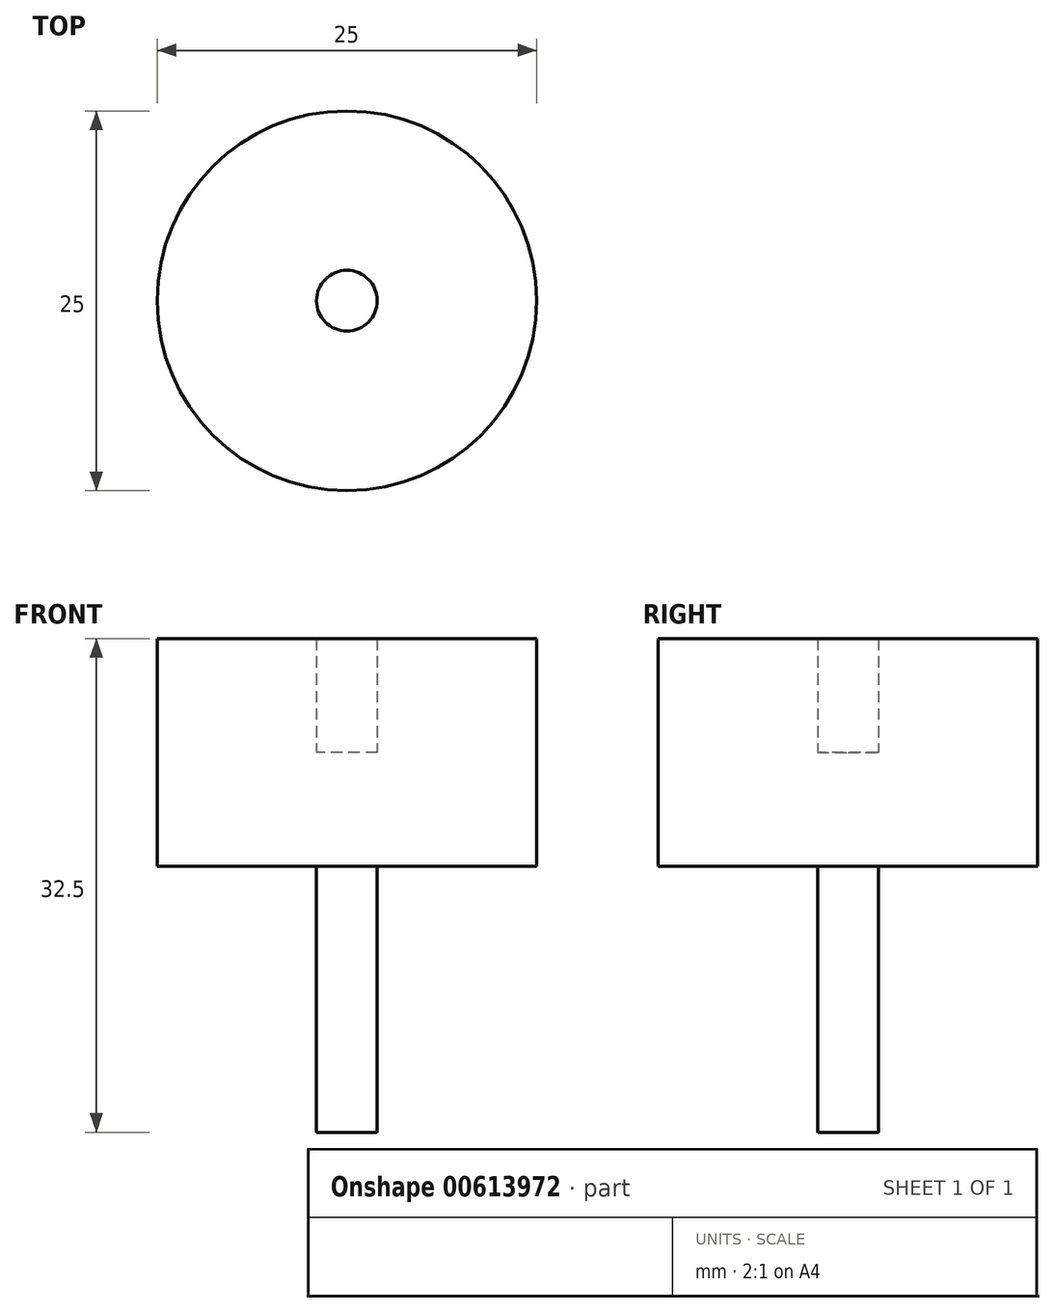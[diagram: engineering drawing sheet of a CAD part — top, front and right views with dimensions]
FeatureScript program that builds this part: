
annotation { "Feature Type Name" : "Feature", "Feature Type Description" : "" }
export const myFeature = defineFeature(function(context is Context, id is Id, definition is map)
    precondition{}
    {
        {
            var Q0;
            Q0=qCreatedBy(makeId("Top.planeOp"),FACE);
            var sketch = newSketch(context, id + "F0", { "sketchPlane" : qUnion([Q0])});
            skCircle(sketch, "E0", {"center": v(0, 0) * mm, "radius": 2 * mm});
            skSolve(sketch);
        }
        {
            var Q0;
            Q0 = qSketchRegion(id + "F0", true);
            extrude(context, id + "F1", {"entities" : qUnion([Q0]), "depth" : 25 * mm, "offsetDistance" : 25 * mm});
        }
        {
            var Q0;
            Q0=makeQuery(id+"F1.opExtrude","CAP_FACE",FACE,{"disambiguationData":[OSD([sQuery(id+"F0.wireOp",EDGE,"E0")])],"isStart":false});
            var sketch = newSketch(context, id + "F2", { "sketchPlane" : qUnion([Q0])});
            skCircle(sketch, "E1", {"center": v(0, 0) * mm, "radius": 12.5 * mm});
            skSolve(sketch);
        }
        {
            var Q0;
            Q0=makeQuery(id+"F2.imprint","IMPRINT",FACE,{"disambiguationData":[TD([[makeQuery(id+"F2.imprint","IMPRINT",EDGE,{"derivedFrom":sQuery(id+"F2.wireOp",EDGE,"E1")}),1.0]])]});
            extrude(context, id + "F3", {"entities" : qUnion([Q0]), "operationType" : NewBodyOperationType.ADD, "endBound" : BoundingType.SYMMETRIC, "depth" : 15 * mm, "offsetDistance" : 25 * mm});
        }
    });
